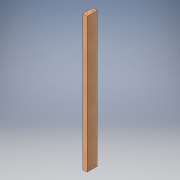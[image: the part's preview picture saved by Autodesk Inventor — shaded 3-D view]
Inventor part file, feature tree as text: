
AUTODESK INVENTOR PART (.ipt)
format: ipt  version: 2016 (Build 200138000, 138)  size: 125,952 bytes
history: native  units: in
note: dims shown in document units (in); Inventor stores cm internally (conversion verified against a paired STEP export)
features: extrude x3, sketch x3
ambient origin geometry x8: Origin, YZ Plane, XZ Plane, XY Plane, X Axis, Y Axis, Z Axis, Center Point
bodies: Solid1 (feature_tree)
feature tree (6):
  extrude  "Wood"  Depth=3.5in
  extrude  "Extrusion4"  Depth=46.5in
  extrude  "Extrusion5"  Depth=1.5in
  sketch  "Sketch1"  dims[d0=1.5in d1=3.5in]
  sketch  "Sketch4"  dims[d2=46.5in d3=0.0in d11=0.1875in]
  sketch  "Sketch5"  dims[d12=1.5in d13=0.0in d14=1.5in d15=0.1875in d16=1.5in d17=0.0in]
